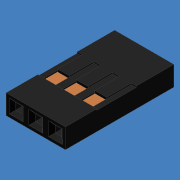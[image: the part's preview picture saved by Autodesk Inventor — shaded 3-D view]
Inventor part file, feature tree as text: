
AUTODESK INVENTOR PART (.ipt)
format: ipt  version: 2012 (Build 160160000, 160)  size: 217,600 bytes
history: native  units: mm (DEFAULTED — no unit token found)
features: extrude x6, sketch x6, projected_geometry x4
ambient origin geometry x8: Origin, YZ Plane, XZ Plane, XY Plane, X Axis, Y Axis, Z Axis, Center Point
bodies: Solid1 (feature_tree)
feature tree (16):
  extrude  "Extrusion1"  Depth=7.62mm
  extrude  "Extrusion2"  Depth=0.381mm
  extrude  "Extrusion3"  Depth=0.381mm
  extrude  "Extrusion4"  Depth=1.778mm
  sketch  "Sketch5"  dims[d9=1.778mm d10=0.762mm]
  extrude  "Extrusion6"  Depth=0.762mm
  extrude  "Extrusion7"  Depth=0.381mm
  sketch  "Sketch6"  dims[d11=0.762mm d12=0.381mm d13=-8.726646mm d14=2.54mm d15=0.0mm d16=1.905mm d17=3.175mm d18=0.0mm d19=5.08mm d21=1.524mm d23=0.889mm d24=0.889mm d25=0.635mm d30=3.175mm d31=4.064mm d32=0.3175mm d33=0.0mm d34=0.15875mm d35=0.0mm]
  sketch  "Sketch1"  dims[d0=2.54mm d1=7.62mm]
  sketch  "Sketch2"  dims[d2=13.97mm d3=0.0mm d4=0.381mm]
  sketch  "Sketch3"  dims[d5=0.381mm d6=0.381mm]
  projected_geometry  "Projected Loop1"
  projected_geometry  "Projected Loop2"
  sketch  "Sketch4"  dims[d7=1.778mm d8=1.778mm]
  projected_geometry  "Projected Loop3"
  projected_geometry  "Projected Loop4"
